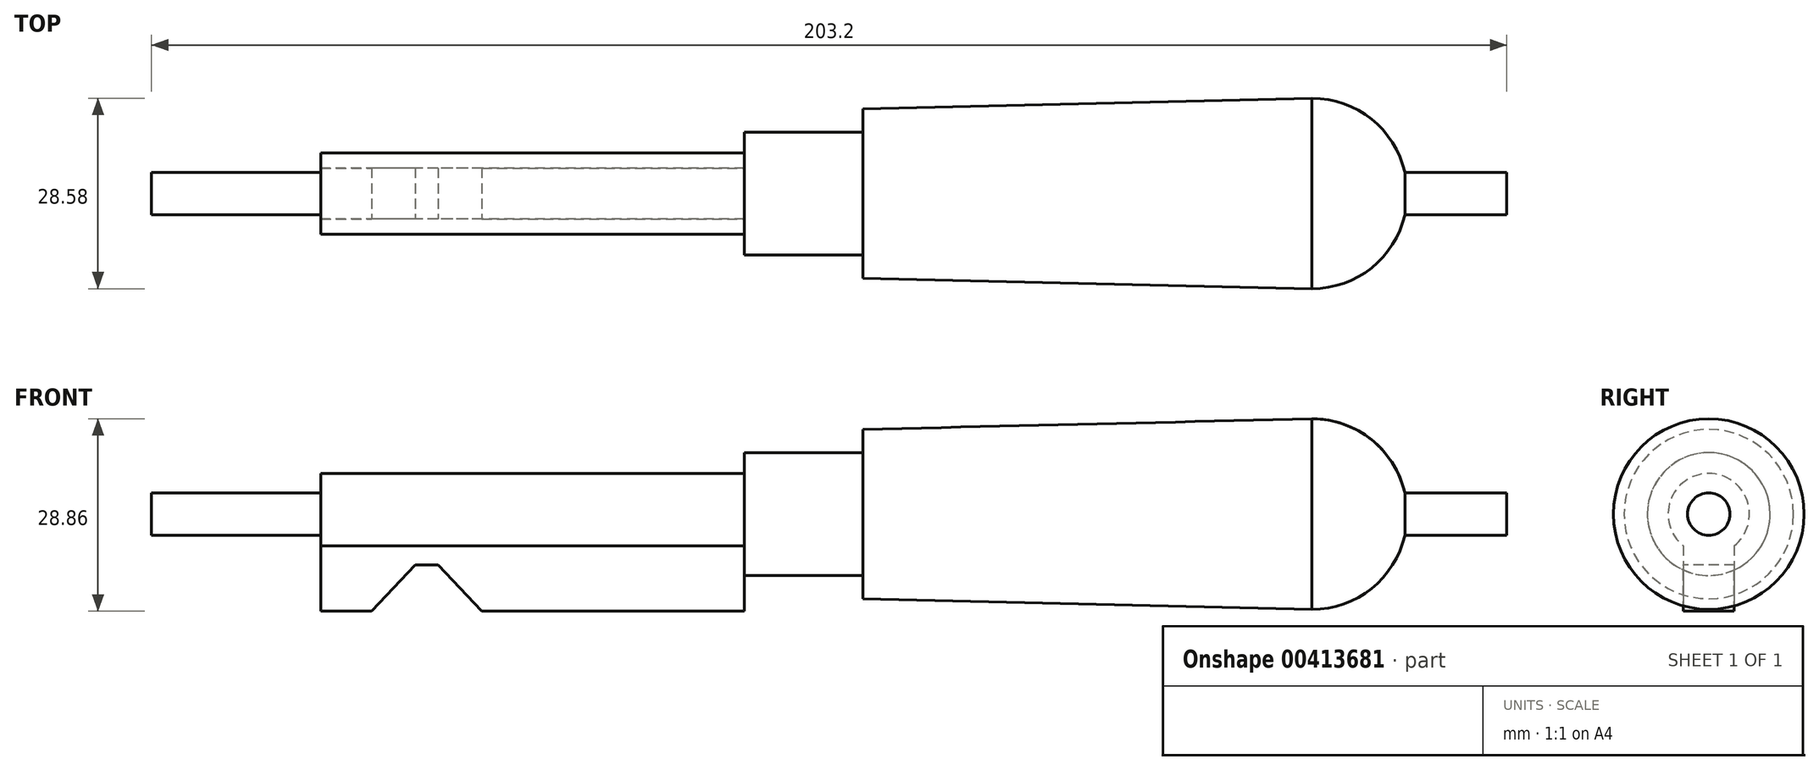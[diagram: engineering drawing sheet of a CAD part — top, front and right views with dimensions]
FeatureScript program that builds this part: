
annotation { "Feature Type Name" : "Feature", "Feature Type Description" : "" }
export const myFeature = defineFeature(function(context is Context, id is Id, definition is map)
    precondition{}
    {
        {
            var Q0;
            Q0=qCreatedBy(makeId("Front.planeOp"),FACE);
            var sketch = newSketch(context, id + "F0", { "sketchPlane" : qUnion([Q0])});
            skLineSegment(sketch, "E0", {"start": v(0, 0) * mm, "end": v(148.6, 0) * mm, "construction": true});
            skArc(sketch, "E1", {"start": v(162.88, 0) * mm, "mid": v(158.7, 10.1) * mm, "end": v(148.6, 14.29) * mm, "construction": true});
            skLineSegment(sketch, "E2", {"start": v(148.6, 14.29) * mm, "end": v(81.28, 12.7) * mm});
            skLineSegment(sketch, "E3", {"start": v(81.28, 12.7) * mm, "end": v(81.28, 9.2) * mm});
            skLineSegment(sketch, "E4", {"start": v(81.28, 9.2) * mm, "end": v(63.5, 9.2) * mm});
            skLineSegment(sketch, "E5", {"start": v(63.5, 9.2) * mm, "end": v(63.5, 6.1) * mm});
            skLineSegment(sketch, "E6", {"start": v(63.5, 6.1) * mm, "end": v(0, 6.1) * mm});
            skLineSegment(sketch, "E7", {"start": v(0, 0) * mm, "end": v(0, 6.1) * mm});
            skLineSegment(sketch, "E8", {"start": v(0, 0) * mm, "end": v(148.6, 0) * mm});
            skLineSegment(sketch, "E9", {"start": v(148.6, 0) * mm, "end": v(148.6, 14.29) * mm});
            skLineSegment(sketch, "E10", {"start": v(148.6, 0) * mm, "end": v(162.88, 0) * mm, "construction": true});
            skSolve(sketch);
        }
        {
            var Q0;
            Q0 = qSketchRegion(id + "F0", true);
            var Q1;
            Q1=sQuery(id+"F0.wireOp",EDGE,"E8");
            revolve(context, id + "F1", {"entities" : qUnion([Q0]), "axis" : qUnion([Q1]), "revolveType" : RevolveType.FULL});
        }
        {
            var Q0;
            Q0=qCreatedBy(makeId("Front.planeOp"),FACE);
            var sketch = newSketch(context, id + "F2", { "sketchPlane" : qUnion([Q0])});
            skLineSegment(sketch, "E11", {"start": v(0, 6.1) * mm, "end": v(63.5, 6.1) * mm, "construction": true});
            skLineSegment(sketch, "E12.bottom", {"start": v(0, 0) * mm, "end": v(63.5, 0) * mm});
            skLineSegment(sketch, "E12.top", {"start": v(0, -14.57) * mm, "end": v(63.5, -14.57) * mm});
            skLineSegment(sketch, "E12.left", {"start": v(0, 0) * mm, "end": v(0, -14.57) * mm});
            skLineSegment(sketch, "E12.right", {"start": v(63.5, 0) * mm, "end": v(63.5, -14.57) * mm});
            skSolve(sketch);
        }
        {
            var Q0;
            Q0 = qSketchRegion(id + "F2", true);
            extrude(context, id + "F3", {"entities" : qUnion([Q0]), "operationType" : NewBodyOperationType.ADD, "depth" : 3.8 * mm, "hasSecondDirection" : true, "secondDirectionOppositeDirection" : true, "secondDirectionDepth" : 3.8 * mm});
        }
        {
            var Q0;
            Q0=makeQuery(id+"F3.opExtrude","CAP_FACE",FACE,{"disambiguationData":[OSD([sQuery(id+"F2.wireOp",EDGE,"E12.bottom"),sQuery(id+"F2.wireOp",EDGE,"E12.top"),sQuery(id+"F2.wireOp",EDGE,"E12.left"),sQuery(id+"F2.wireOp",EDGE,"E12.right")])],"isStart":false});
            var sketch = newSketch(context, id + "F4", { "sketchPlane" : qUnion([Q0])});
            skLineSegment(sketch, "E13", {"start": v(7.62, -14.57) * mm, "end": v(24.13, -14.57) * mm});
            skLineSegment(sketch, "E14", {"start": v(24.13, -14.57) * mm, "end": v(17.59, -7.62) * mm});
            skLineSegment(sketch, "E15", {"start": v(17.59, -7.62) * mm, "end": v(14.16, -7.62) * mm});
            skLineSegment(sketch, "E16", {"start": v(14.16, -7.62) * mm, "end": v(7.62, -14.57) * mm});
            skLineSegment(sketch, "E17", {"start": v(15.88, -14.57) * mm, "end": v(15.88, -7.62) * mm});
            skSolve(sketch);
        }
        {
            var Q0;
            Q0 = qSketchRegion(id + "F4", true);
            extrude(context, id + "F5", {"entities" : qUnion([Q0]), "operationType" : NewBodyOperationType.REMOVE, "endBound" : BoundingType.THROUGH_ALL, "oppositeDirection" : true, "depth" : 25.4 * mm});
        }
        {
            var Q0;
            Q0=qCreatedBy(makeId("Front.planeOp"),FACE);
            var sketch = newSketch(context, id + "F6", { "sketchPlane" : qUnion([Q0])});
            skLineSegment(sketch, "E18", {"start": v(162.88, 0) * mm, "end": v(148.6, 0) * mm});
            skLineSegment(sketch, "E19", {"start": v(148.6, 0) * mm, "end": v(148.6, 14.29) * mm});
            skArc(sketch, "E20", {"start": v(148.6, 14.29) * mm, "mid": v(158.7, 10.1) * mm, "end": v(162.88, 0) * mm});
            skSolve(sketch);
        }
        {
            var Q0;
            Q0 = qSketchRegion(id + "F6", true);
            var Q1;
            Q1=sQuery(id+"F6.wireOp",EDGE,"E18");
            revolve(context, id + "F7", {"entities" : qUnion([Q0]), "axis" : qUnion([Q1]), "revolveType" : RevolveType.FULL});
        }
        {
            var Q0;
            Q0=makeQuery(id+"F7.opRevolve","SWEPT_BODY",BODY,{"disambiguationData":[OSD([sQuery(id+"F6.wireOp",EDGE,"E18"),sQuery(id+"F6.wireOp",EDGE,"E19"),sQuery(id+"F6.wireOp",EDGE,"E20")])]});
            deleteBodies(context, id + "F8", {"entities" : qUnion([Q0])});
        }
        {
            var Q0;
            Q0 = qSketchRegion(id + "F6", true);
            var Q1;
            Q1=sQuery(id+"F0.wireOp",EDGE,"E10");
            revolve(context, id + "F9", {"operationType" : NewBodyOperationType.ADD, "entities" : qUnion([Q0]), "axis" : qUnion([Q1]), "revolveType" : RevolveType.FULL});
        }
        {
            var Q0;
            Q0=qCreatedBy(makeId("Front.planeOp"),FACE);
            var sketch = newSketch(context, id + "F10", { "sketchPlane" : qUnion([Q0])});
            skLineSegment(sketch, "E21.bottom", {"start": v(-25.4, 0) * mm, "end": v(177.8, 0) * mm});
            skLineSegment(sketch, "E21.top", {"start": v(-25.4, 3.18) * mm, "end": v(177.8, 3.18) * mm});
            skLineSegment(sketch, "E21.left", {"start": v(-25.4, 0) * mm, "end": v(-25.4, 3.18) * mm});
            skLineSegment(sketch, "E21.right", {"start": v(177.8, 0) * mm, "end": v(177.8, 3.18) * mm});
            skSolve(sketch);
        }
        {
            var Q0;
            Q0 = qSketchRegion(id + "F10", true);
            var Q1;
            Q1=sQuery(id+"F10.wireOp",EDGE,"E21.bottom");
            revolve(context, id + "F11", {"operationType" : NewBodyOperationType.ADD, "entities" : qUnion([Q0]), "axis" : qUnion([Q1]), "revolveType" : RevolveType.FULL});
        }
    });
